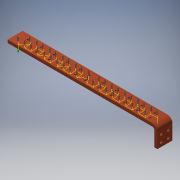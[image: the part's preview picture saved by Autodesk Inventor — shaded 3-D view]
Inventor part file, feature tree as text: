
AUTODESK INVENTOR PART (.ipt)
format: ipt  version: 2016 SP2 (Build 200236200, 236)  size: 470,016 bytes
history: native  units: mm
features: reference x21, sketch x6, hole x4, pattern_linear x4, extrude x1, other x1, projected_geometry x1
ambient origin geometry x8: Origin, YZ Plane, XZ Plane, XY Plane, X Axis, Y Axis, Z Axis, Center Point
bodies: Solid1 (feature_tree)
feature tree (38):
  extrude  "Extrusion1"  Depth=6.0mm
  other  "Bend Part1"
  hole  "Hole1"  [1 undecoded]
  hole  "Hole2"  [1 undecoded]
  pattern_linear  "Rectangular Pattern1"  Spacing1=6.0mm  [1 undecoded]
  pattern_linear  "Rectangular Pattern2"  Count1=6 Spacing1=26.0mm
  hole  "Hole4"  [1 undecoded]
  hole  "Hole5"  [1 undecoded]
  pattern_linear  "Rectangular Pattern4"  Spacing1=15.0mm  [1 undecoded]
  pattern_linear  "Rectangular Pattern5"  Spacing1=15.0mm  [1 undecoded]
  sketch  "Sketch1"  dims[d0=30.0mm d1=6.0mm]
  sketch  "Sketch2"  dims[d2=335.0mm d3=0.0mm d4=305.0mm]
  projected_geometry  "Projected Loop1"
  sketch  "Sketch4"  dims[d5=10.0mm d6=90.0deg]
  reference  "Reference7"
  reference  "Reference8"
  reference  "Reference9"
  reference  "Reference10"
  reference  "Reference11"
  reference  "Reference12"
  reference  "Reference13"
  reference  "Reference14"
  reference  "Reference15"
  reference  "Reference16"
  reference  "Reference17"
  reference  "Reference18"
  reference  "Reference19"
  reference  "Reference20"
  reference  "Reference21"
  reference  "Reference22"
  reference  "Reference23"
  reference  "Reference24"
  reference  "Reference25"
  reference  "Reference26"
  sketch  "Sketch5"  dims[d7=1.567mm d8=5.0mm d9=4.0mm d10=2.0mm d11=90.0deg d12=6.0mm d13=20.594885mm d14=7.0mm]
  reference  "Reference27"
  sketch  "Sketch10"  dims[d16=9.7mm d17=6.0mm d18=3.242mm d19=5.0mm d20=4.0mm d21=2.0mm d22=90.0deg d23=5.0mm d24=20.594885mm d25=60.0mm d27=26.0mm d28=20.0mm d30=150.0mm d52=14.0mm d53=14.0mm d56=15.0mm d57=15.0mm d58=5.3mm d59=5.0mm d60=4.0mm d61=2.0mm d62=90.0deg d63=5.0mm d64=20.594885mm d65=1.8mm d66=6.0mm d67=4.0mm d68=2.0mm d69=90.0deg d70=4.0mm d71=20.594885mm d72=100.0mm d74=13.0mm d75=20.0mm d77=137.3mm d78=6.0mm d79=8.6mm]
  sketch  "Sketch9"  dims[d15=10.0mm]
note: 7 required parameter values undecoded (feature->parameter linkage not recoverable at this tier; creation-order binding heuristic only, values carry confidence <= 0.55)
